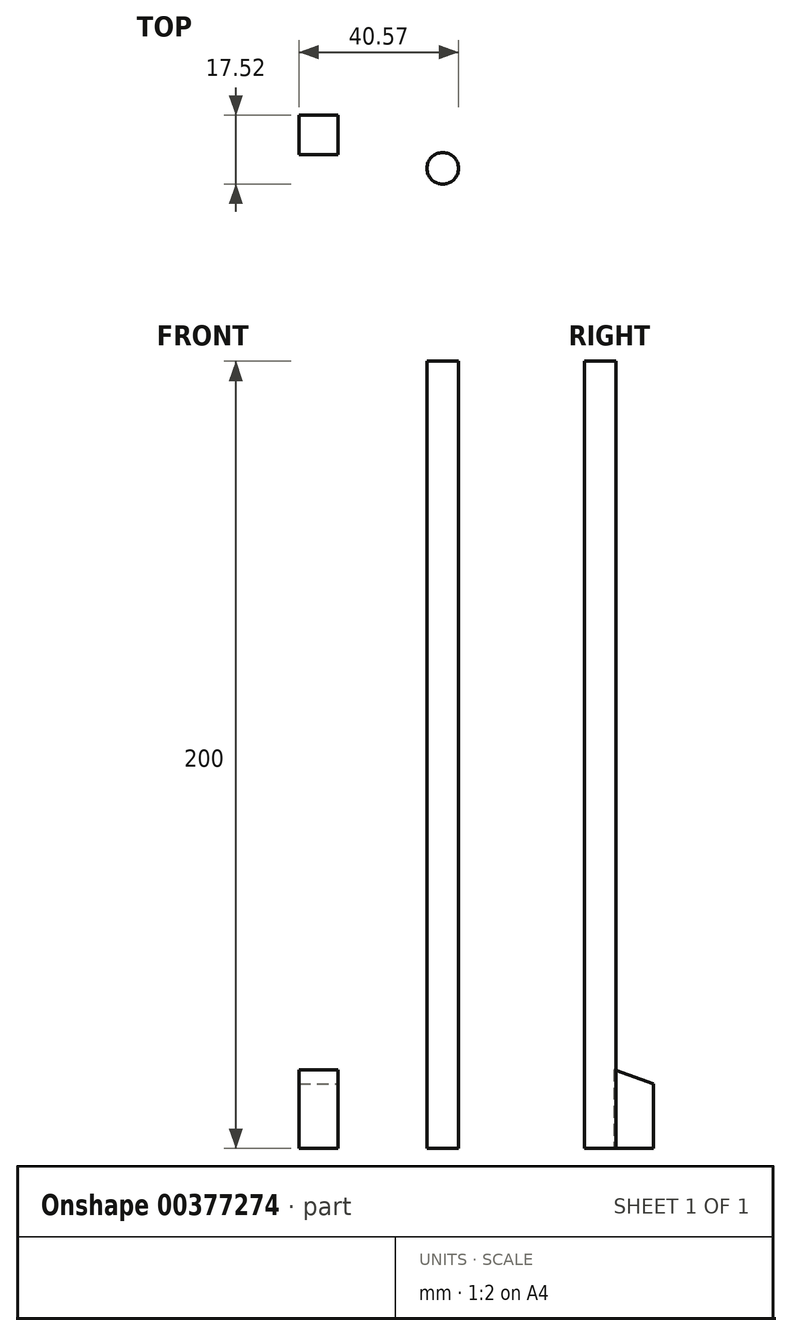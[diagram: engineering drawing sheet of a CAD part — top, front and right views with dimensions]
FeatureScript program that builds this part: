
annotation { "Feature Type Name" : "Feature", "Feature Type Description" : "" }
export const myFeature = defineFeature(function(context is Context, id is Id, definition is map)
    precondition{}
    {
        {
            var Q0;
            Q0=qCreatedBy(makeId("Top.planeOp"),FACE);
            var sketch = newSketch(context, id + "F0", { "sketchPlane" : qUnion([Q0])});
            skCircle(sketch, "E0", {"center": v(0, 0) * mm, "radius": 4 * mm});
            skSolve(sketch);
        }
        {
            var Q0;
            Q0 = qSketchRegion(id + "F0", true);
            extrude(context, id + "F1", {"entities" : qUnion([Q0]), "depth" : 200 * mm});
        }
        {
            var Q0;
            Q0=qCreatedBy(makeId("Top.planeOp"),FACE);
            var sketch = newSketch(context, id + "F2", { "sketchPlane" : qUnion([Q0])});
            skLineSegment(sketch, "E1.bottom", {"start": v(-36.57, 13.52) * mm, "end": v(-26.57, 13.52) * mm});
            skLineSegment(sketch, "E1.top", {"start": v(-36.57, 3.52) * mm, "end": v(-26.57, 3.52) * mm});
            skLineSegment(sketch, "E1.left", {"start": v(-36.57, 13.52) * mm, "end": v(-36.57, 3.52) * mm});
            skLineSegment(sketch, "E1.right", {"start": v(-26.57, 13.52) * mm, "end": v(-26.57, 3.52) * mm});
            skSolve(sketch);
        }
        {
            var Q0;
            Q0=makeQuery(id+"F2.imprint","IMPRINT",FACE,{"disambiguationData":[TD([[makeQuery(id+"F2.imprint","IMPRINT",EDGE,{"derivedFrom":sQuery(id+"F2.wireOp",EDGE,"E1.bottom")}),-1.0]])]});
            extrude(context, id + "F3", {"entities" : qUnion([Q0]), "depth" : 20 * mm});
        }
        {
            var Q0;
            Q0=makeQuery(id+"F3.opExtrude","CAP_EDGE",EDGE,{"disambiguationData":[OSD([sQuery(id+"F2.wireOp",EDGE,"E1.bottom")])],"isStart":false});
            chamfer(context, id + "F4", {"entities" : qUnion([Q0]), "chamferType" : ChamferType.OFFSET_ANGLE, "width" : 10 * mm, "oppositeDirection" : true, "angle" : 20 * degree, "tangentPropagation" : true});
        }
    });
